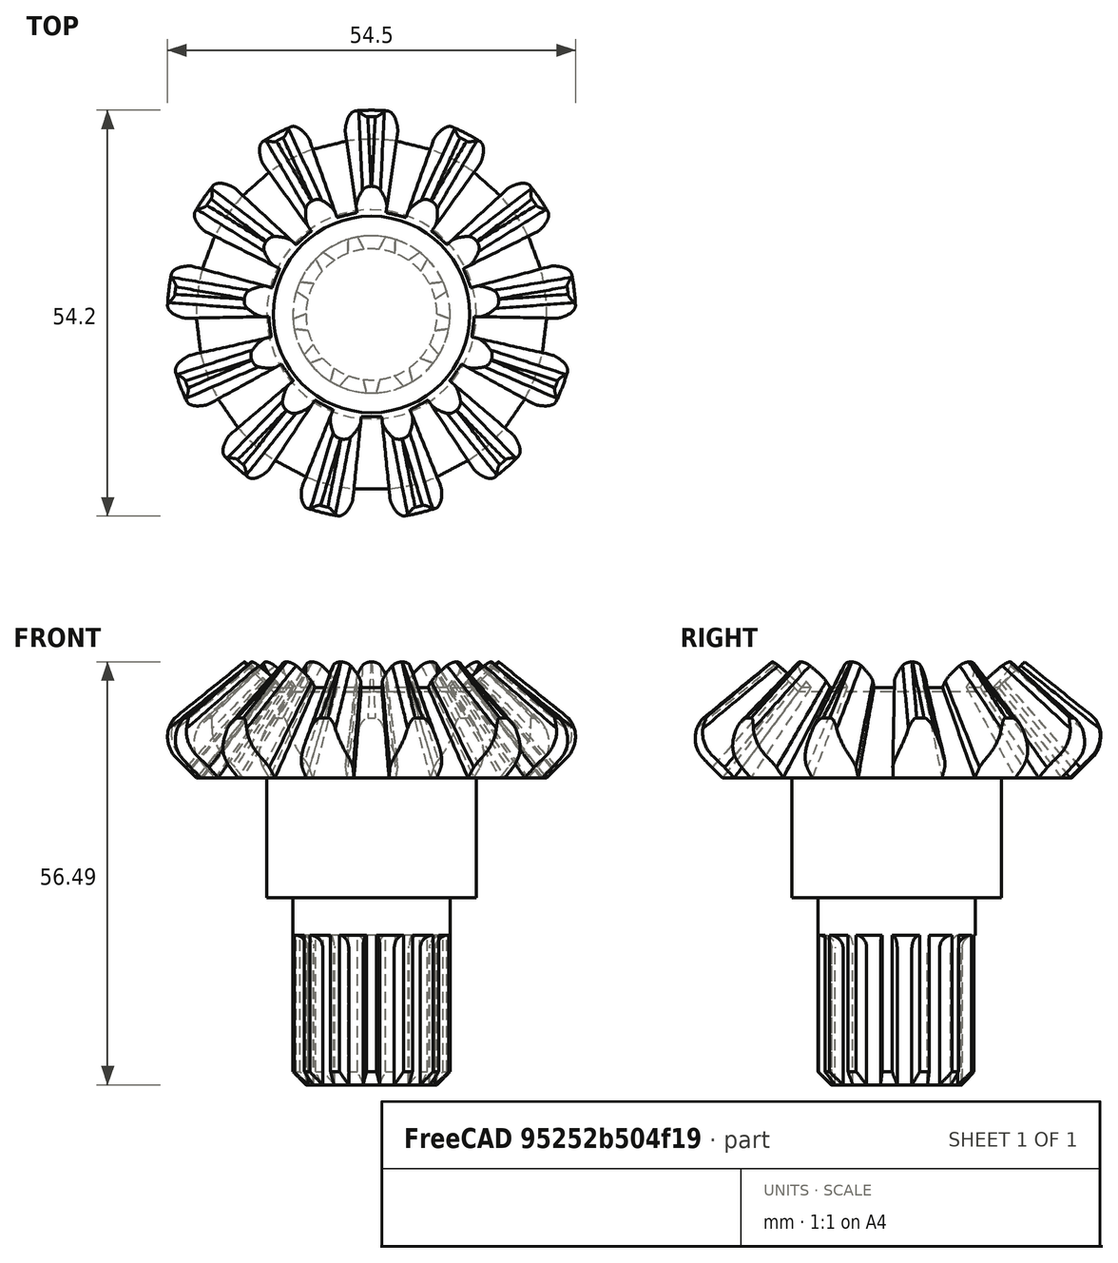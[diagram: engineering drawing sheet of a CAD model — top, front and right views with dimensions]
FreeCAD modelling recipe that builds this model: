
FCSTD DOCUMENT  (FreeCAD 1.0R39319 (Git))
Label: DG Krushna Straight miter gear2
License: All rights reserved
LicenseURL: https://en.wikipedia.org/wiki/All_rights_reserved
objects: Sketcher::SketchObject×11, TechDraw::DrawViewDimension×5, PartDesign::Groove×4, PartDesign::Pad×3, TechDraw::DrawProjGroupItem×3, PartDesign::Fillet×2, Part::FeaturePython×1, PartDesign::FeatureBase×1, PartDesign::Pocket×1, PartDesign::PolarPattern×1, PartDesign::Chamfer×1, PartDesign::Body×1, TechDraw::DrawSVGTemplate×1, TechDraw::DrawProjGroup×1, TechDraw::DrawPage×1
note: 66 computed .brp shape members not serialized (recipe doc carries the construction recipe); baked Part::Feature solids carry a one-line shape summary decoded from their .brp

FEATURE [Part::FeaturePython] BevelGear  # WARN: FeaturePython — macro-defined, semantics opaque (R4)
  AttacherType = Attacher::AttachEngine3D
  angular_backlash = 0
  backlash = 0
  beta = 0
  clearance = 0.1
  dw = 58.5
  height = 15.5
  module = 4.5
  num_teeth = 13
  numpoints = 20
  pitch_angle = 45
  pressure_angle = 20
  reset_origin = true
  version = 1.3.0
  expr: angular_backlash = backlash / dw * 360 ° / pi
  expr: dw = num_teeth * module
FEATURE [PartDesign::FeatureBase] BaseFeature
  BaseFeature = -> BevelGear
  Suppressed = false
FEATURE [Sketcher::SketchObject] Sketch
  ArcFitTolerance = 1e-06
  AttachmentSupport = -> [BaseFeature]
  ExternalGeometry = -> [BaseFeature]
  FullyConstrained = true
  MakeInternals = false
  MapMode = 5
  Placement = pos=(0,0,0) rot=(1,0,0;3.14159rad)
  sketch-geometry (2):
    g0: Circle CenterX=0 CenterY=0 CenterZ=0 NormalX=0 NormalY=0 NormalZ=1 AngleXU=0 Radius=23.3992
    g1: Circle CenterX=0 CenterY=0 CenterZ=0 NormalX=0 NormalY=0 NormalZ=1 AngleXU=0 Radius=36.4225
  constraints (4):
    c: Coincident(g0,g-1)
    c: PointOnObject(g-4,g0)
    c: Coincident(g1,g0)
    c: PointOnObject(g-3,g1)
FEATURE [Sketcher::SketchObject] Sketch001
  ArcFitTolerance = 1e-06
  AttachmentSupport = -> [YZ_Plane]
  ExternalGeometry = -> [Sketch]
  FullyConstrained = true
  MakeInternals = false
  MapMode = 5
  Placement = pos=(0,0,0) rot=(0.57735,0.57735,0.57735;2.0944rad)
  sketch-geometry (3):
    g0: LineSegment StartX=23.3992 StartY=0 StartZ=0 EndX=36.4225 EndY=13.0233 EndZ=0
    g1: LineSegment StartX=36.4225 StartY=0 StartZ=0 EndX=36.4225 EndY=13.0233 EndZ=0
    g2: LineSegment StartX=23.3992 StartY=0 StartZ=0 EndX=36.4225 EndY=0 EndZ=0
  constraints (7):
    c: Coincident(g0,g-3)
    c: Coincident(g1,g-4)
    c: Vertical(g1)
    c: Coincident(g0,g1)
    c: Angle(g-4,g0) = 0.785398
    c: Coincident(g2,g0)
    c: Coincident(g2,g1)
FEATURE [PartDesign::Groove] Groove
  Angle = 360
  Angle2 = 60
  Axis = (0,0,1)
  Base = (0,0,0)
  BaseFeature = -> BaseFeature
  Profile = -> Sketch001
  ReferenceAxis = -> Sketch001 [V_Axis]
  Refine = true
  Suppressed = false
  Type = 0
FEATURE [Sketcher::SketchObject] Sketch002
  ArcFitTolerance = 1e-06
  AttachmentSupport = -> [Groove]
  ExternalGeometry = -> [Groove]
  FullyConstrained = true
  MakeInternals = false
  MapMode = 5
  Placement = pos=(-3e-16,-5e-16,15.5) rot=(0,0,1;0rad)
  sketch-geometry (2):
    g0: Circle CenterX=0 CenterY=0 CenterZ=0 NormalX=0 NormalY=0 NormalZ=1 AngleXU=0 Radius=10.9996
    g1: Circle CenterX=0 CenterY=0 CenterZ=0 NormalX=0 NormalY=0 NormalZ=1 AngleXU=0 Radius=17.1217
  constraints (4):
    c: Coincident(g0,g-1)
    c: PointOnObject(g-3,g0)
    c: Coincident(g1,g0)
    c: PointOnObject(g-4,g1)
FEATURE [Sketcher::SketchObject] Sketch003
  ArcFitTolerance = 1e-06
  AttachmentSupport = -> [YZ_Plane]
  ExternalGeometry = -> [Sketch002]
  FullyConstrained = true
  MakeInternals = false
  MapMode = 5
  Placement = pos=(0,0,0) rot=(0.57735,0.57735,0.57735;2.0944rad)
  sketch-geometry (4):
    g0: LineSegment StartX=17.1217 StartY=15.5 StartZ=0 EndX=13.1217 EndY=11.5 EndZ=0
    g1: LineSegment StartX=13.1217 StartY=11.5 StartZ=0 EndX=0 EndY=11.5 EndZ=0
    g2: LineSegment StartX=0 StartY=11.5 StartZ=0 EndX=2e-16 EndY=15.5 EndZ=0
    g3: LineSegment StartX=7e-16 StartY=15.5 StartZ=0 EndX=17.1217 EndY=15.5 EndZ=0
  constraints (10):
    c: Coincident(g0,g-4)
    c: Coincident(g1,g0)
    c: PointOnObject(g1,g-2)
    c: Horizontal(g1)
    c: Coincident(g2,g1)
    c: Symmetric(g-4,g-4,g2)
    c: Symmetric(g-4,g-4,g3)
    c: Coincident(g3,g0)
    c: Angle(g3,g0) = 0.785398
    c: Distance(g3,g1) = 4
FEATURE [Sketcher::SketchObject] Sketch005
  ArcFitTolerance = 1e-06
  AttachmentSupport = -> [Groove]
  ExternalGeometry = -> [Groove]
  FullyConstrained = true
  MakeInternals = false
  MapMode = 5
  Placement = pos=(-3e-16,-5e-16,15.5) rot=(0,0,1;0rad)
  constraints (1):
    c: Distance(g-3,g-3) = 2.20134
FEATURE [PartDesign::Groove] Groove001
  Angle = 360
  Angle2 = 60
  Axis = (0,0,1)
  Base = (0,0,0)
  BaseFeature = -> Groove
  Profile = -> Sketch003
  ReferenceAxis = -> Sketch003 [V_Axis]
  Refine = true
  Suppressed = false
  Type = 0
FEATURE [Sketcher::SketchObject] Sketch006
  ArcFitTolerance = 1e-06
  AttachmentSupport = -> [Groove001]
  FullyConstrained = true
  MakeInternals = false
  MapMode = 5
  Placement = pos=(0,0,0) rot=(1,0,0;3.14159rad)
  sketch-geometry (1):
    g0: Circle CenterX=0 CenterY=0 CenterZ=0 NormalX=0 NormalY=0 NormalZ=1 AngleXU=0 Radius=14
  constraints (2):
    c: Diameter(g0) = 28
    c: Coincident(g0,g-1)
FEATURE [PartDesign::Pad] Pad
  BaseFeature = -> Groove001
  Direction = (0,0,-1)
  Length = 16
  Length2 = 10
  Profile = -> Sketch006
  ReferenceAxis = -> Sketch006 [N_Axis]
  Refine = true
  Suppressed = false
  Type = 0
FEATURE [Sketcher::SketchObject] Sketch009
  ArcFitTolerance = 1e-06
  AttachmentSupport = -> [YZ_Plane]
  FullyConstrained = true
  MakeInternals = false
  MapMode = 5
  Placement = pos=(0,0,0) rot=(0.57735,0.57735,0.57735;2.0944rad)
  sketch-geometry (5):
    g0: ArcOfCircle CenterX=29.7006 CenterY=6.73825 CenterZ=0 NormalX=0 NormalY=0 NormalZ=1 AngleXU=0 Radius=4 StartAngle=5.49779 EndAngle=7.17681
    g1: LineSegment StartX=37.529 StartY=3.90983 StartZ=0 EndX=32.529 EndY=3.90983 EndZ=0
    g2: LineSegment StartX=32.207 StartY=9.85564 StartZ=0 EndX=37.529 EndY=9.85564 EndZ=0
    g3: LineSegment StartX=37.529 StartY=9.85564 StartZ=0 EndX=37.529 EndY=3.90983 EndZ=0
    g4: LineSegment [constr] StartX=17.1129 StartY=21.9912 StartZ=0 EndX=35.6814 EndY=7.0622 EndZ=0
  constraints (13):
    c: Tangent(g0,g-3) = -1.5708
    c: Radius(g0) = 4
    c: Coincident(g1,g0)
    c: Coincident(g0,g2)
    c: Coincident(g2,g3)
    c: Coincident(g1,g3)
    c: Horizontal(g2)
    c: Horizontal(g1)
    c: Vertical(g3)
    c: DistanceX(g1,g1) = 5
    c: Coincident(g4,g-4)
    c: Coincident(g4,g-3)
    c: Tangent(g0,g4) = 1.5708
FEATURE [PartDesign::Groove] Groove002
  Angle = 360
  Angle2 = 60
  Axis = (0,0,1)
  Base = (0,0,0)
  BaseFeature = -> Pad
  Profile = -> Sketch009
  ReferenceAxis = -> Sketch009 [V_Axis]
  Refine = true
  Suppressed = false
  Type = 0
FEATURE [Sketcher::SketchObject] Sketch010
  ArcFitTolerance = 1e-06
  AttachmentSupport = -> [Groove002]
  FullyConstrained = true
  MakeInternals = false
  MapMode = 5
  Placement = pos=(0,0,-16) rot=(1,0,0;3.14159rad)
  sketch-geometry (1):
    g0: Circle CenterX=0 CenterY=0 CenterZ=0 NormalX=0 NormalY=0 NormalZ=1 AngleXU=0 Radius=10.5
  constraints (2):
    c: Diameter(g0) = 21
    c: Coincident(g0,g-1)
FEATURE [PartDesign::Pad] Pad001
  BaseFeature = -> Groove002
  Direction = (0,0,-1)
  Length = 25
  Length2 = 10
  Profile = -> Sketch010
  ReferenceAxis = -> Sketch010 [N_Axis]
  Refine = true
  Suppressed = false
  Type = 0
FEATURE [Sketcher::SketchObject] Sketch011
  ArcFitTolerance = 1e-06
  AttachmentSupport = -> [Pad001]
  ExternalGeometry = -> [Pad001]
  FullyConstrained = true
  MakeInternals = false
  MapMode = 5
  Placement = pos=(0,0,-41) rot=(1,0,0;3.14159rad)
  sketch-geometry (2):
    g0: Circle CenterX=0 CenterY=0 CenterZ=0 NormalX=0 NormalY=0 NormalZ=1 AngleXU=0 Radius=8.75
    g1: Circle CenterX=0 CenterY=0 CenterZ=0 NormalX=0 NormalY=0 NormalZ=1 AngleXU=0 Radius=15
  constraints (4):
    c: Diameter(g0) = 17.5
    c: Coincident(g0,g-1)
    c: Coincident(g1,g0)
    c: Diameter(g1) = 30
FEATURE [PartDesign::Pocket] Pocket
  BaseFeature = -> Pad001
  Direction = (0,0,1)
  Length = 20
  Length2 = 5
  Profile = -> Sketch011
  ReferenceAxis = -> Sketch011 [N_Axis]
  Refine = true
  Suppressed = false
  Type = 0
FEATURE [Sketcher::SketchObject] Sketch012
  ArcFitTolerance = 1e-06
  AttachmentSupport = -> [Pocket]
  ExternalGeometry = -> [Pocket]
  FullyConstrained = true
  MakeInternals = false
  MapMode = 5
  Placement = pos=(0,0,-41) rot=(1,0,0;3.14159rad)
  sketch-geometry (7):
    g0: LineSegment StartX=-1.1189 StartY=8.67817 StartZ=0 EndX=-0.67 EndY=10.4786 EndZ=0
    g1: LineSegment StartX=1.1189 StartY=8.67817 StartZ=0 EndX=0.67 EndY=10.4786 EndZ=0
    g2: LineSegment [constr] StartX=-4.914 StartY=11.9363 StartZ=0 EndX=-4.914 EndY=1.4269 EndZ=0
    g3: LineSegment [constr] StartX=5.37904 StartY=12.0909 StartZ=0 EndX=5.37904 EndY=1.30326 EndZ=0
    g4: ArcOfCircle CenterX=0 CenterY=0 CenterZ=0 NormalX=0 NormalY=0 NormalZ=1 AngleXU=0 Radius=10.5 StartAngle=1.50694 EndAngle=1.63465
    g5: ArcOfCircle CenterX=0 CenterY=0 CenterZ=0 NormalX=0 NormalY=0 NormalZ=1 AngleXU=0 Radius=8.75 StartAngle=1.44257 EndAngle=1.69902
    g6: LineSegment [constr] StartX=-0.89445 StartY=9.57838 StartZ=0 EndX=0.89445 EndY=9.57838 EndZ=0
  constraints (18):
    c: PointOnObject(g0,g-3)
    c: PointOnObject(g0,g-4)
    c: Equal(g0,g1)
    c: Vertical(g2)
    c: Vertical(g3)
    c: Angle(g0,g2) = 0.244346
    c: Coincident(g4,g-1)
    c: Coincident(g4,g0)
    c: Coincident(g4,g1)
    c: Distance(g0,g1) = 1.34
    c: Coincident(g5,g0)
    c: Coincident(g5,g1)
    c: Coincident(g5,g4)
    c: Block(g3)
    c: Block(g2)
    c: Symmetric(g0,g0,g6)
    c: Symmetric(g1,g1,g6)
    c: Horizontal(g6)
FEATURE [PartDesign::Pad] Pad002
  BaseFeature = -> Pocket
  Direction = (0,0,-1)
  Length = 20
  Length2 = 10
  Profile = -> Sketch012
  ReferenceAxis = -> Sketch012 [N_Axis]
  Refine = true
  Reversed = true
  Suppressed = false
  Type = 0
FEATURE [PartDesign::PolarPattern] PolarPattern
  Angle = 360
  Axis = -> Sketch012 [N_Axis]
  BaseFeature = -> Pad002
  Mode = 0
  Occurrences = 13
  Offset = 120
  Originals = -> [Pad002]
  Refine = true
  Suppressed = false
  TransformMode = 0
FEATURE [PartDesign::Chamfer] Chamfer
  Angle = 45
  Base = -> PolarPattern [Edge52,Edge56,Edge48,Edge44,Edge40,Edge36,Edge60,Edge12,Edge16,Edge20,Edge24,Edge28,Edge32]
  BaseFeature = -> PolarPattern
  ChamferType = 0
  FlipDirection = false
  Refine = true
  Size = 1.75
  Size2 = 1
  SupportTransform = false
  Suppressed = false
  UseAllEdges = false
FEATURE [PartDesign::Fillet] Fillet
  Base = -> Chamfer [Edge62,Edge71,Edge79,Edge95,Edge111,Edge127,Edge140,Edge152,Edge157,Edge132,Edge116,Edge100,Edge84]
  BaseFeature = -> Chamfer
  Radius = 1.74
  Refine = true
  SupportTransform = false
  Suppressed = false
  UseAllEdges = false
FEATURE [Sketcher::SketchObject] Sketch013
  ArcFitTolerance = 1e-06
  AttachmentSupport = -> [YZ_Plane]
  ExternalGeometry = -> [Fillet]
  FullyConstrained = true
  MakeInternals = false
  MapMode = 5
  Placement = pos=(0,0,0) rot=(0.57735,0.57735,0.57735;2.0944rad)
  sketch-geometry (9):
    g0: ArcOfCircle CenterX=23.2751 CenterY=5.53269 CenterZ=0 NormalX=0 NormalY=0 NormalZ=1 AngleXU=0 Radius=4 StartAngle=5.49779 EndAngle=7.17681
    g1: ArcOfCircle [constr] CenterX=17.102 CenterY=15.5 CenterZ=0 NormalX=0 NormalY=0 NormalZ=-1 AngleXU=-2.46442 Radius=0.1 StartAngle=1.5708 EndAngle=4.71239
    g2: LineSegment [constr] StartX=17.1647 StartY=15.5779 StartZ=0 EndX=21.1923 EndY=12.3398 EndZ=0
    g3: LineSegment [constr] StartX=21.1923 StartY=12.3398 StartZ=0 EndX=29.2474 EndY=5.86345 EndZ=0
    g4: ArcOfCircle [constr] CenterX=29.1847 CenterY=5.78552 CenterZ=0 NormalX=0 NormalY=0 NormalZ=-1 AngleXU=0.677174 Radius=0.1 StartAngle=1.5708 EndAngle=4.71239
    g5: LineSegment [constr] StartX=21.0669 StartY=12.1839 StartZ=0 EndX=29.1221 EndY=5.70758 EndZ=0
    g6: LineSegment [constr] StartX=17.0394 StartY=15.4221 StartZ=0 EndX=21.0669 EndY=12.1839 EndZ=0
    g7: LineSegment StartX=25.7814 StartY=8.65008 StartZ=0 EndX=29.2559 EndY=5.85664 EndZ=0
    g8: LineSegment StartX=26.1035 StartY=2.70427 StartZ=0 EndX=29.2559 EndY=5.85664 EndZ=0
  constraints (15):
    c: Radius(g0) = 4
    c: Tangent(g0,g-3) = -1.5708
    c: Tangent(g1,g2) = 1.5708
    c: Tangent(g1,g6) = -1.5708
    c: Coincident(g2,g3)
    c: Coincident(g5,g6)
    c: Block(g3)
    c: Block(g5)
    c: Block(g4)
    c: Block(g1)
    c: Block(g6)
    c: Tangent(g0,g3) = 1.5708
    c: Tangent(g7,g0) = 1.5708
    c: Tangent(g8,g0) = -1.5708
    c: Coincident(g7,g8)
FEATURE [PartDesign::Groove] Groove003
  Angle = 360
  Angle2 = 60
  Axis = (0,0,1)
  Base = (0,0,0)
  BaseFeature = -> Fillet
  Profile = -> Sketch013
  ReferenceAxis = -> Sketch013 [V_Axis]
  Refine = true
  Suppressed = false
  Type = 0
FEATURE [PartDesign::Fillet] Fillet001
  Base = -> Groove003 [Edge502,Edge498,Edge484,Edge488,Edge470,Edge474,Edge456,Edge460,Edge442,Edge446,Edge430,Edge427,Edge508,Edge503,Edge494,Edge489,Edge480,Edge475,Edge466,Edge461,Edge452,Edge447,Edge438,Edge433,Edge423,Edge418]
  BaseFeature = -> Groove003
  Radius = 1.3
  Refine = true
  SupportTransform = false
  Suppressed = false
  UseAllEdges = false
FEATURE [PartDesign::Body] Body  label="miter gear 2"
  AllowCompound = false
  BaseFeature = -> BevelGear
  Group = -> [BaseFeature,Sketch,Sketch001,Groove,Sketch002,Sketch003,Sketch005,Groove001,Sketch006,Pad,Sketch009,Groove002,Sketch010,Pad001,Sketch011,Pocket,Sketch012,Pad002,PolarPattern,Chamfer,Fillet,Sketch013,Groove003,Fillet001]
  Origin = -> Origin
  Tip = -> Fillet001
FEATURE [TechDraw::DrawSVGTemplate] Template
  EditableTexts = AuthorName=Krushna Manwatkar; CheckDate=CHECK DATE; CreationDate=06-01-2026; DrawingNumber=NUMBER; FC-Title=DG Krushna Straight miter gear2; SheetNumber=1 / 1; Subtitle=SUBTITLE; SupervisorName=SUPERVISOR NAME; Weight=WEIGHT; scale=1 : 1
  Height = 297
  Orientation = 1
  Template = C:/Program Files/FreeCAD 1.0/data/Mod/TechDraw/Templates/A3_Landscape_TD.svg
  Width = 420
FEATURE [TechDraw::DrawProjGroupItem] View  label="Front"
  CoarseView = false
  Direction = (0,-1,0)
  Focus = 100
  HardHidden = false
  IsoCount = 0
  IsoHidden = false
  IsoVisible = false
  LockPosition = true
  Perspective = false
  Rotation = 0
  RotationVector = (1,0,0)
  ScaleType = 2
  ScrubCount = 1
  SeamHidden = false
  SeamVisible = false
  SmoothHidden = false
  SmoothVisible = true
  Source = -> [Body]
  Type = 0
  X = 0
  XDirection = (1,0,0)
  Y = 0
FEATURE [TechDraw::DrawProjGroupItem] ProjItem  label="Bottom"
  CoarseView = false
  Direction = (0,0,-1)
  Focus = 100
  HardHidden = false
  IsoCount = 0
  IsoHidden = false
  IsoVisible = false
  LockPosition = false
  Perspective = false
  Rotation = 0
  RotationVector = (1,0,0)
  ScaleType = 0
  ScrubCount = 1
  SeamHidden = false
  SeamVisible = false
  SmoothHidden = false
  SmoothVisible = true
  Source = -> [Body]
  Type = 5
  X = 0
  XDirection = (1,0,0)
  Y = -73.7662
FEATURE [TechDraw::DrawProjGroupItem] ProjItem002  label="FrontBottomRight"
  CoarseView = false
  Direction = (0.57735,-0.57735,-0.57735)
  Focus = 100
  HardHidden = false
  IsoCount = 0
  IsoHidden = false
  IsoVisible = false
  LockPosition = false
  Perspective = false
  Rotation = 0
  RotationVector = (1,0,0)
  ScaleType = 0
  ScrubCount = 1
  SeamHidden = false
  SeamVisible = false
  SmoothHidden = false
  SmoothVisible = true
  Source = -> [Body]
  Type = 9
  X = 69.4541
  XDirection = (0.707107,0.707107,0)
  Y = -73.7662
FEATURE [TechDraw::DrawProjGroup] ProjGroup
  Anchor = -> View
  AutoDistribute = true
  LockPosition = false
  ProjectionType = 1
  Rotation = 0
  ScaleType = 0
  Source = -> [Body]
  Views = -> [View,ProjItem,ProjItem002]
  X = 189.137
  Y = 202.007
  spacingX = 15
  spacingY = 15
FEATURE [TechDraw::DrawViewDimension] Dimension
  AngleOverride = false
  Arbitrary = false
  ArbitraryTolerances = false
  BoxCorners = (2) [(-27.2515,-28.2456,-1e-07),(27.2499,28.2456,1e-07)]
  EqualTolerance = true
  ExtensionAngle = 0
  FormatSpec = %.2w
  FormatSpecOverTolerance = %+.2w
  FormatSpecUnderTolerance = %+.2w
  Inverted = false
  LineAngle = 0
  LockPosition = false
  MeasureType = 1
  OverTolerance = 0
  References2D = -> [View]
  Rotation = 0
  ScaleType = 0
  TheoreticalExact = false
  Type = 0
  UnderTolerance = 0
  X = 57.0331
  Y = -2.03183
FEATURE [TechDraw::DrawViewDimension] Dimension001
  AngleOverride = false
  Arbitrary = false
  ArbitraryTolerances = false
  BoxCorners = (2) [(-27.2515,-28.2456,-1e-07),(27.2499,28.2456,1e-07)]
  EqualTolerance = true
  ExtensionAngle = 0
  FormatSpec = %.2w
  FormatSpecOverTolerance = %+.2w
  FormatSpecUnderTolerance = %+.2w
  Inverted = false
  LineAngle = 0
  LockPosition = false
  MeasureType = 1
  OverTolerance = 0
  References2D = -> [View]
  Rotation = 0
  ScaleType = 0
  TheoreticalExact = false
  Type = 2
  UnderTolerance = 0
  X = 114.867
  Y = 4.75437
FEATURE [TechDraw::DrawViewDimension] Dimension002
  AngleOverride = false
  Arbitrary = false
  ArbitraryTolerances = false
  BoxCorners = (2) [(-27.2515,-28.2456,-1e-07),(27.2499,28.2456,1e-07)]
  EqualTolerance = true
  ExtensionAngle = 0
  FormatSpec = %.2w
  FormatSpecOverTolerance = %+.2w
  FormatSpecUnderTolerance = %+.2w
  Inverted = false
  LineAngle = 0
  LockPosition = false
  MeasureType = 1
  OverTolerance = 0
  References2D = -> [View]
  Rotation = 0
  ScaleType = 0
  TheoreticalExact = false
  Type = 0
  UnderTolerance = 0
  X = 127.626
  Y = -35.1511
FEATURE [TechDraw::DrawViewDimension] Dimension003
  AngleOverride = false
  Arbitrary = false
  ArbitraryTolerances = false
  BoxCorners = (2) [(-27.2499,-27.0959,-1e-07),(27.2499,27.0959,1e-07)]
  EqualTolerance = true
  ExtensionAngle = 0
  FormatSpec = %.2w
  FormatSpecOverTolerance = %+.2w
  FormatSpecUnderTolerance = %+.2w
  Inverted = false
  LineAngle = 0
  LockPosition = false
  MeasureType = 1
  OverTolerance = 0
  References2D = -> [ProjItem]
  Rotation = 0
  ScaleType = 0
  TheoreticalExact = false
  Type = 0
  UnderTolerance = 0
  X = -40.8955
  Y = 28.4073
FEATURE [TechDraw::DrawViewDimension] Dimension004
  AngleOverride = false
  Arbitrary = false
  ArbitraryTolerances = false
  BoxCorners = (2) [(-27.2499,-27.0959,-1e-07),(27.2499,27.0959,1e-07)]
  EqualTolerance = true
  ExtensionAngle = 0
  FormatSpec = ⌀%.2w
  FormatSpecOverTolerance = %+.2w
  FormatSpecUnderTolerance = %+.2w
  Inverted = false
  LineAngle = 0
  LockPosition = false
  MeasureType = 1
  OverTolerance = 0
  References2D = -> [ProjItem]
  Rotation = 0
  ScaleType = 0
  TheoreticalExact = false
  Type = 5
  UnderTolerance = 0
  X = -53.6328
  Y = -18.4446
FEATURE [TechDraw::DrawPage] Page
  KeepUpdated = true
  NextBalloonIndex = 1
  ProjectionType = 0
  Template = -> Template
  Views = -> [ProjGroup,Dimension,Dimension001,Dimension002,Dimension003,Dimension004]
